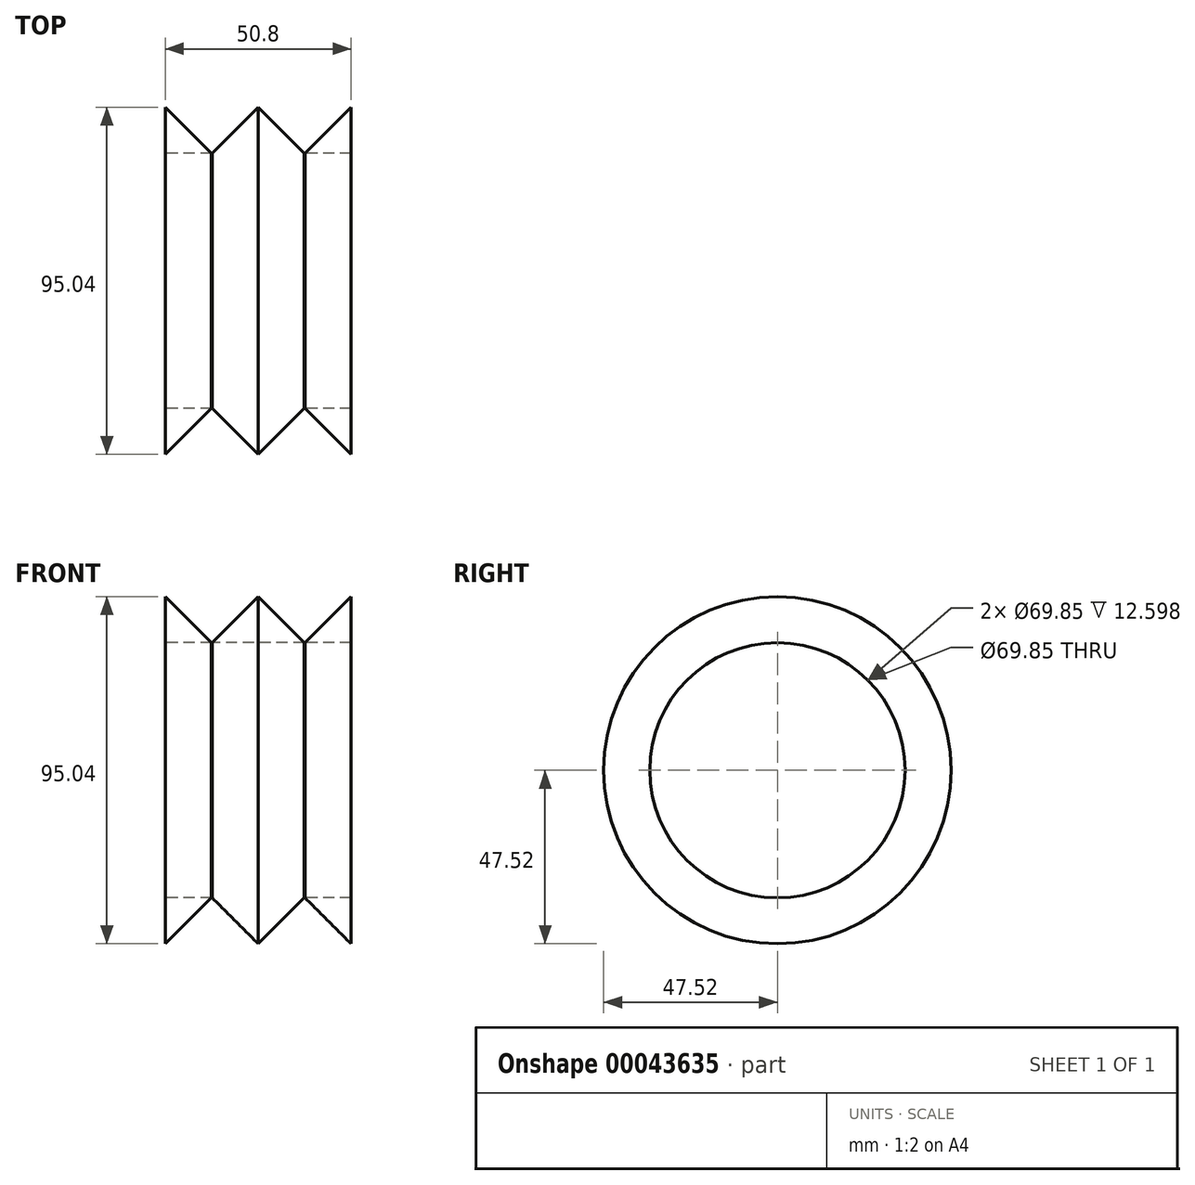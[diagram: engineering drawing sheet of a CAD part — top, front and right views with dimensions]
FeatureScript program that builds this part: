
annotation { "Feature Type Name" : "Feature", "Feature Type Description" : "" }
export const myFeature = defineFeature(function(context is Context, id is Id, definition is map)
    precondition{}
    {
        {
            var Q0;
            Q0=qCreatedBy(makeId("Front.planeOp"),FACE);
            var sketch = newSketch(context, id + "F0", { "sketchPlane" : qUnion([Q0])});
            skLineSegment(sketch, "E0", {"start": v(0, 0) * mm, "end": v(104.57, 0) * mm});
            skLineSegment(sketch, "E1", {"start": v(0, 22.12) * mm, "end": v(50.8, 22.12) * mm});
            skLineSegment(sketch, "E2", {"start": v(50.8, 22.12) * mm, "end": v(50.8, 47.52) * mm});
            skLineSegment(sketch, "E3", {"start": v(50.8, 47.52) * mm, "end": v(38.1, 34.82) * mm});
            skLineSegment(sketch, "E4", {"start": v(38.1, 34.82) * mm, "end": v(25.4, 47.52) * mm});
            skLineSegment(sketch, "E5", {"start": v(25.4, 47.52) * mm, "end": v(12.7, 34.82) * mm});
            skLineSegment(sketch, "E6", {"start": v(12.7, 34.82) * mm, "end": v(0, 47.52) * mm});
            skLineSegment(sketch, "E7", {"start": v(0, 22.12) * mm, "end": v(0, 47.52) * mm});
            skLineSegment(sketch, "E8", {"start": v(12.7, 34.82) * mm, "end": v(12.7, 22.12) * mm});
            skLineSegment(sketch, "E9", {"start": v(38.1, 34.82) * mm, "end": v(38.1, 22.12) * mm});
            skSolve(sketch);
        }
        {
            var Q0;
            Q0 = qSketchRegion(id + "F0", true);
            var Q1;
            Q1=sQuery(id+"F0.wireOp",EDGE,"E0");
            revolve(context, id + "F1", {"entities" : qUnion([Q0]), "axis" : qUnion([Q1]), "revolveType" : RevolveType.FULL});
        }
        {
            var Q0;
            Q0=qCreatedBy(makeId("Right.planeOp"),FACE);
            var sketch = newSketch(context, id + "F2", { "sketchPlane" : qUnion([Q0])});
            skCircle(sketch, "E10", {"center": v(0, 0) * mm, "radius": 34.93 * mm});
            skCircle(sketch, "E11", {"center": v(0, 0) * mm, "radius": 12.7 * mm});
            skSolve(sketch);
        }
        {
            var Q0;
            Q0=makeQuery(id+"F2.imprint","IMPRINT",FACE,{"disambiguationData":[TD([[makeQuery(id+"F2.imprint","IMPRINT",EDGE,{"derivedFrom":sQuery(id+"F2.wireOp",EDGE,"E10")}),1.0]])]});
            extrude(context, id + "F3", {"entities" : qUnion([Q0]), "operationType" : NewBodyOperationType.REMOVE, "endBound" : BoundingType.THROUGH_ALL, "depth" : 25.4 * mm});
        }
    });
